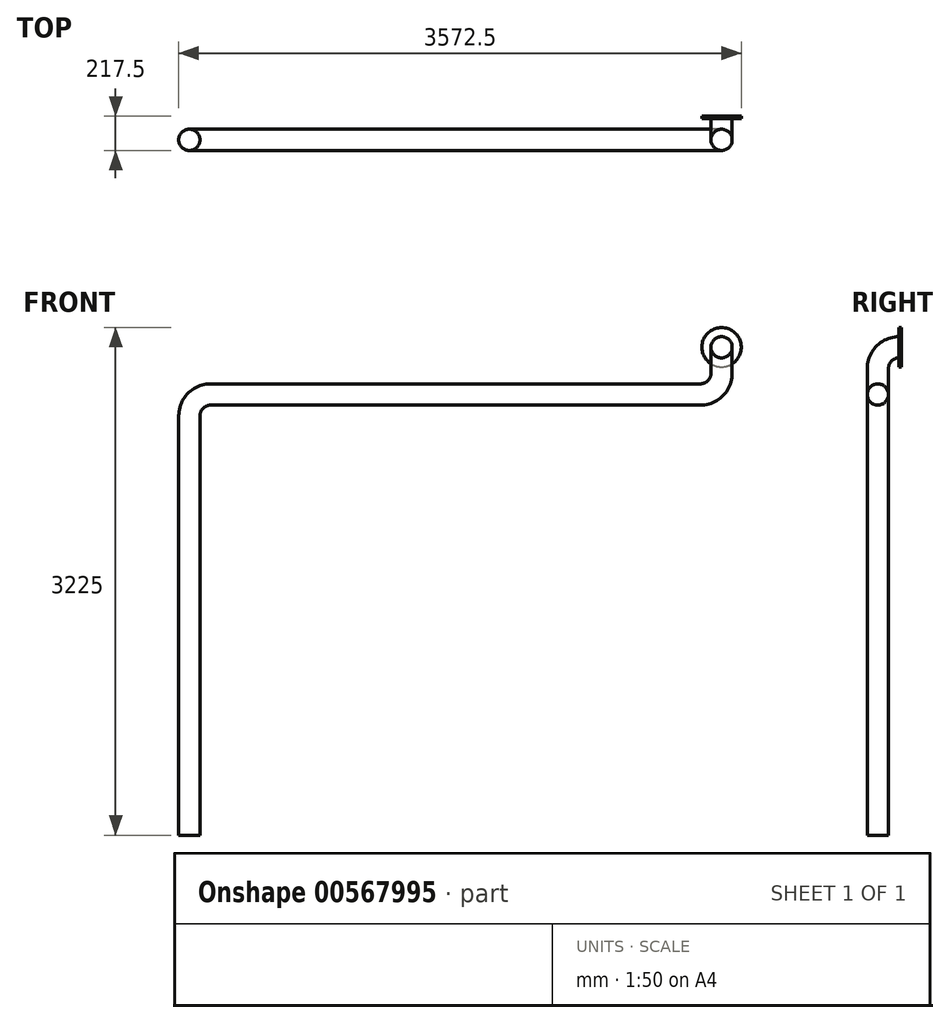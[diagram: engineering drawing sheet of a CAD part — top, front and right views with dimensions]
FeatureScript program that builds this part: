
annotation { "Feature Type Name" : "Feature", "Feature Type Description" : "" }
export const myFeature = defineFeature(function(context is Context, id is Id, definition is map)
    precondition{}
    {
        {
            var Q0;
            Q0=qCreatedBy(makeId("Front.planeOp"),FACE);
            var sketch = newSketch(context, id + "F0", { "sketchPlane" : qUnion([Q0])});
            skCircle(sketch, "E0", {"center": v(0, 0) * mm, "radius": 67.5 * mm});
            skCircle(sketch, "E1", {"center": v(0, 0) * mm, "radius": 125 * mm});
            skSolve(sketch);
        }
        {
            var Q0;
            Q0=qCreatedBy(makeId("Right.planeOp"),FACE);
            var sketch = newSketch(context, id + "F1", { "sketchPlane" : qUnion([Q0])});
            skLineSegment(sketch, "E2", {"start": v(0, 0) * mm, "end": v(-15, 0) * mm});
            skLineSegment(sketch, "E3", {"start": v(-150, -135) * mm, "end": v(-150, -150) * mm});
            skPoint(sketch, "E4.visualSharp", {"position": v(-150, 0) * mm});
            skArc(sketch, "E4.filletArc", {"start": v(-15, 0) * mm, "mid": v(-110.46, -39.54) * mm, "end": v(-150, -135) * mm});
            skSolve(sketch);
        }
        {
            var Q0;
            Q0=qCreatedBy(makeId("Front.planeOp"),FACE);
            cPlane(context, id + "F2", {"entities" : qUnion([Q0]), "cplaneType" : CPlaneType.OFFSET, "offset" : 150 * mm, "width" : 150 * mm, "height" : 150 * mm});
        }
        {
            var Q0;
            Q0=qCreatedBy(id+"F2.planeOp",FACE);
            var sketch = newSketch(context, id + "F3", { "sketchPlane" : qUnion([Q0])});
            skLineSegment(sketch, "E5.0", {"start": v(0, -135) * mm, "end": v(0, -150) * mm});
            skLineSegment(sketch, "E6", {"start": v(0, -150) * mm, "end": v(0, -165) * mm});
            skLineSegment(sketch, "E7", {"start": v(-135, -300) * mm, "end": v(-3245, -300) * mm});
            skLineSegment(sketch, "E8", {"start": v(-3380, -435) * mm, "end": v(-3380, -3100) * mm});
            skPoint(sketch, "E9.visualSharp", {"position": v(0, -300) * mm});
            skArc(sketch, "E9.filletArc", {"start": v(-135, -300) * mm, "mid": v(-39.54, -260.46) * mm, "end": v(0, -165) * mm});
            skPoint(sketch, "E10.visualSharp", {"position": v(-3380, -300) * mm});
            skArc(sketch, "E10.filletArc", {"start": v(-3245, -300) * mm, "mid": v(-3340.46, -339.54) * mm, "end": v(-3380, -435) * mm});
            skSolve(sketch);
        }
        {
            var Q0;
            Q0=makeQuery(id+"F0.imprint","IMPRINT",FACE,{"disambiguationData":[TD([[makeQuery(id+"F0.imprint","IMPRINT",EDGE,{"derivedFrom":sQuery(id+"F0.wireOp",EDGE,"E0")}),1.0]])]});
            var Q1;
            Q1=sQuery(id+"F1.wireOp",EDGE,"E2");
            var Q2;
            Q2=sQuery(id+"F1.wireOp",EDGE,"E4.filletArc");
            var Q3;
            Q3=sQuery(id+"F3.wireOp",EDGE,"E5.0");
            var Q4;
            Q4=sQuery(id+"F3.wireOp",EDGE,"E6");
            var Q5;
            Q5=sQuery(id+"F3.wireOp",EDGE,"E9.filletArc");
            var Q6;
            Q6=sQuery(id+"F3.wireOp",EDGE,"E7");
            var Q7;
            Q7=sQuery(id+"F3.wireOp",EDGE,"E10.filletArc");
            var Q8;
            Q8=sQuery(id+"F3.wireOp",EDGE,"E8");
            sweep(context, id + "F4", {"profiles" : qUnion([Q0]), "path" : qUnion([Q1, Q2, Q3, Q4, Q5, Q6, Q7, Q8])});
        }
        {
            var Q0;
            Q0=makeQuery(id+"F0.imprint","IMPRINT",FACE,{"disambiguationData":[TD([[makeQuery(id+"F0.imprint","IMPRINT",EDGE,{"derivedFrom":sQuery(id+"F0.wireOp",EDGE,"E0")}),-1.0]])]});
            extrude(context, id + "F5", {"entities" : qUnion([Q0]), "operationType" : NewBodyOperationType.ADD, "depth" : 15 * mm, "offsetDistance" : 25 * mm});
        }
    });
